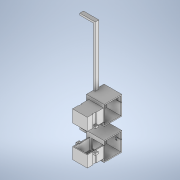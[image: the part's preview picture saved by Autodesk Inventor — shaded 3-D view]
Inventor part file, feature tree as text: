
AUTODESK INVENTOR PART (.ipt)
format: ipt  version: 2020.2 (Build 242310000, 310)  size: 759,296 bytes
history: native  units: mm
features: sketch x35, extrude x34, projected_geometry x11, hole x2
ambient origin geometry x8: Origin, YZ Plane, XZ Plane, XY Plane, X Axis, Y Axis, Z Axis, Center Point
bodies: Solid1 (feature_tree)
feature tree (82):
  sketch  "Sketch1"  dims[d0=29.0mm d1=35.0mm]
  extrude  "Extrusion1"  Depth=35.0mm
  extrude  "Extrusion2"  Depth=2.0mm
  extrude  "Extrusion3"  Depth=39.0mm
  hole  "Hole1"  [1 undecoded]
  extrude  "Extrusion4"  Depth=10.0mm
  sketch  "Sketch5"  dims[d10=10.0mm d11=0.0mm d12=4.2mm]
  sketch  "Sketch6"  dims[d13=4.475mm d14=26.05mm]
  extrude  "Extrusion5"  Depth=26.05mm
  extrude  "Extrusion6"  Depth=39.0mm
  extrude  "Extrusion7"  Depth=33.0mm TaperAngle=0.0deg
  sketch  "Sketch10"  dims[d27=7.0mm d28=7.0mm]
  extrude  "Extrusion8"  Depth=7.0mm
  extrude  "Extrusion9"  Depth=7.0mm
  extrude  "Extrusion14"  Depth=10.0mm
  extrude  "Extrusion15"  Depth=20.0mm
  extrude  "Extrusion16"  Depth=22.5mm
  extrude  "Extrusion17"  Depth=1.0mm
  extrude  "Extrusion18"  Depth=24.0mm
  extrude  "Extrusion19"  Depth=1.0mm
  extrude  "Extrusion25"  Depth=26.0mm
  extrude  "Extrusion26"  Depth=1.0mm
  extrude  "Extrusion27"  Depth=1.0mm
  extrude  "Extrusion28"  Depth=26.0mm TaperAngle=0.0deg
  extrude  "Extrusion29"  Depth=1.0mm TaperAngle=0.0deg
  extrude  "Extrusion30"  Depth=14.0mm
  extrude  "Extrusion31"  TaperAngle=90.0deg  [1 undecoded]
  extrude  "Extrusion32"  Depth=3.5mm
  sketch  "Sketch39"  dims[d82=35.0mm d83=3.5mm]
  extrude  "Extrusion33"  Depth=7.0mm
  extrude  "Extrusion34"  Depth=7.0mm
  extrude  "Extrusion37"  Depth=5.0mm TaperAngle=0.0deg
  extrude  "Extrusion38"  Depth=1.0mm TaperAngle=0.0deg
  sketch  "Sketch43"  dims[d88=3.4mm d89=5.0mm d90=0.0mm]
  extrude  "Extrusion39"  Depth=1.0mm TaperAngle=0.0deg
  extrude  "Extrusion40"  Depth=16.0mm
  extrude  "Extrusion42"  Depth=1.5mm
  extrude  "Extrusion43"  Depth=5.0mm
  hole  "Hole2"  [1 undecoded]
  extrude  "Extrusion44"  Depth=21.0mm
  extrude  "Extrusion45"  Depth=19.5mm
  extrude  "Extrusion46"  Depth=4.0mm
  sketch  "Sketch2"  dims[d2=2.0mm d3=2.0mm]
  sketch  "Sketch3"  dims[d4=33.0mm d5=39.0mm]
  sketch  "Sketch4"  dims[d6=2.0mm d7=0.0mm d8=40.0mm d9=0.0mm]
  sketch  "Sketch7"  dims[d15=29.6mm]
  projected_geometry  "Projected Loop1"
  sketch  "Sketch8"  dims[d16=3.4mm d17=6.0mm d18=6.3mm d19=2.0mm d20=90.0deg d21=8.0mm d22=20.594885mm d23=39.0mm]
  sketch  "Sketch9"  dims[d24=2.0mm d25=33.0mm d26=0.0mm]
  sketch  "Sketch11"  dims[d29=7.0mm d30=7.0mm]
  sketch  "Sketch16"  dims[d31=5.0mm d32=0.0mm d33=10.0mm]
  sketch  "Sketch17"  dims[d34=3.5mm d35=20.0mm]
  sketch  "Sketch18"  dims[d36=90.0deg d37=22.5mm]
  projected_geometry  "Projected Loop4"
  sketch  "Sketch19"  dims[d38=10.0mm d39=0.0mm d40=1.0mm]
  projected_geometry  "Projected Loop5"
  sketch  "Sketch21"  dims[d41=10.0mm d42=0.0mm d43=24.0mm]
  projected_geometry  "Projected Loop6"
  sketch  "Sketch30"  dims[d44=30.48mm d45=1.0mm]
  projected_geometry  "Projected Loop7"
  sketch  "Sketch31"  dims[d46=31.48mm d47=26.0mm]
  projected_geometry  "Projected Loop8"
  sketch  "Sketch32"  dims[d48=34.0mm d49=0.0mm d50=1.0mm]
  projected_geometry  "Projected Loop9"
  projected_geometry  "Projected Loop10"
  sketch  "Sketch34"  dims[d51=29.48mm d52=0.0mm d69=1.0mm]
  sketch  "Sketch35"  dims[d70=35.0mm d71=26.0mm d72=0.0mm]
  sketch  "Sketch36"  dims[d73=10.0mm d74=0.0mm d75=1.0mm d76=0.0mm]
  sketch  "Sketch37"  dims[d77=1.0mm d78=0.0mm d79=14.0mm]
  sketch  "Sketch38"  dims[d80=17.5mm d81=90.0deg]
  projected_geometry  "Projected Loop12"
  sketch  "Sketch40"  dims[d84=7.0mm d85=7.0mm]
  sketch  "Sketch42"  dims[d86=7.0mm d87=3.4mm]
  projected_geometry  "Projected Loop13"
  sketch  "Sketch44"  dims[d91=1.0mm d92=0.0mm d131=1.0mm d132=0.0mm]
  sketch  "Sketch45"  dims[d133=1.0mm d134=0.0mm d135=1.0mm d136=0.0mm]
  sketch  "Sketch46"  dims[d137=1.0mm d138=0.0mm d139=16.0mm]
  sketch  "Sketch47"  dims[d140=10.0mm d141=1.5mm]
  projected_geometry  "Projected Loop14"
  sketch  "Sketch49"  dims[d142=2.0mm d143=5.0mm]
  sketch  "Sketch50"  dims[d144=3.5mm d145=5.5mm]
  sketch  "Sketch51"  dims[d146=10.0mm d147=0.0mm d148=21.0mm d149=19.5mm d150=4.0mm d151=8.0mm d152=4.0mm d153=30.0mm d154=0.0mm d155=4.0mm d156=8.0mm d157=201.358mm d158=0.0mm d159=4.0mm d160=30.0mm d161=0.0mm d162=44.0mm d163=4.0mm d164=39.0mm d165=42.0mm d166=90.0deg d167=39.0mm d168=90.0deg d169=2.0mm d170=2.0mm d171=2.0mm d172=2.0mm d173=4.0mm d174=0.0mm d175=35.0mm d176=0.0mm d177=1.0mm d178=7.0mm d179=25.0mm d180=2.0mm d185=2.0mm d186=36.0mm d187=0.0mm d188=2.0mm d189=28.48mm d190=34.0mm d191=25.0mm d192=0.0mm d193=30.0mm d194=0.0mm d195=5.0mm d196=0.0mm d199=1.0mm d200=0.0mm d201=4.75mm d202=4.2mm d203=26.05mm d204=29.6mm d205=3.4mm d206=6.0mm d207=7.0mm d208=5.0mm d209=90.0deg d210=8.0mm d211=20.594885mm d212=3.0mm d213=0.0mm d214=10.0mm d215=0.0mm d216=2.0mm d217=1.0mm d218=32.0mm d219=0.0mm d220=15.0mm d221=10.0mm d222=2.0mm d223=90.0deg d224=6.5mm d225=10.0mm d226=0.0mm d54=0.5mm d55=0.872665mm d56=0.5mm d57=0.872665mm d58=0.5mm d59=0.872665mm d60=0.5mm d61=0.872665mm d116=0.5mm d117=0.872665mm d118=0.5mm d119=0.872665mm]
note: 3 required parameter values undecoded (feature->parameter linkage not recoverable at this tier; creation-order binding heuristic only, values carry confidence <= 0.55)
